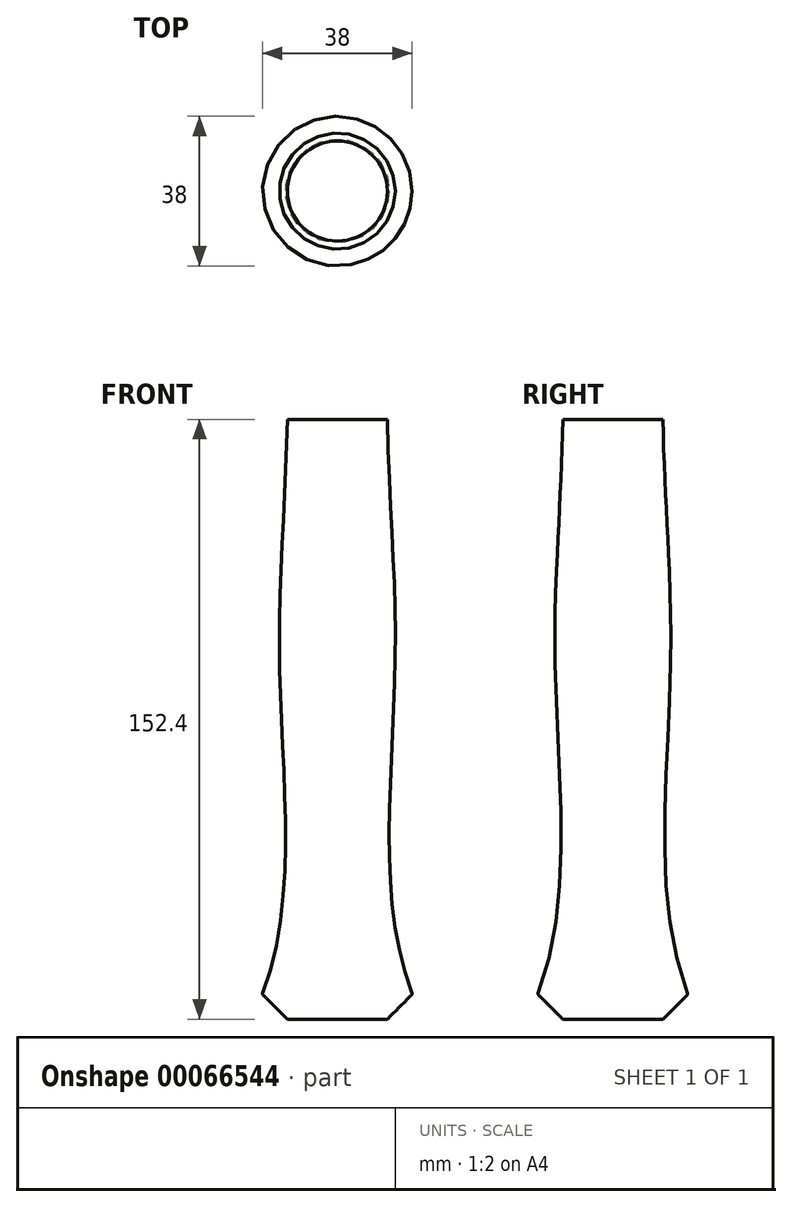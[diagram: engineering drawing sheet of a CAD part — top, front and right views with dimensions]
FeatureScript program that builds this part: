
annotation { "Feature Type Name" : "Feature", "Feature Type Description" : "" }
export const myFeature = defineFeature(function(context is Context, id is Id, definition is map)
    precondition{}
    {
        {
            var Q0;
            Q0=qCreatedBy(makeId("Front.planeOp"),FACE);
            var sketch = newSketch(context, id + "F0", { "sketchPlane" : qUnion([Q0])});
            skLineSegment(sketch, "E0", {"start": v(-26.54, 75.17) * mm, "end": v(-39.24, 75.17) * mm});
            skLineSegment(sketch, "E1", {"start": v(-26.54, -77.23) * mm, "end": v(-39.24, -77.23) * mm});
            skLineSegment(sketch, "E2", {"start": v(-45.6, -70.88) * mm, "end": v(-39.24, -77.23) * mm});
            skFitSpline(sketch, "E3.MirrorCS", {"points": [v(-39.24, 75.17) * mm, v(-41.3, 19.53) * mm, v(-39.72, -29.46) * mm, v(-45.6, -70.88) * mm], "startDerivative": vector(-4.03, -183.72) * mm, "endDerivative": vector(-47.17, -125.03) * mm});
            skLineSegment(sketch, "E4", {"start": v(-26.54, 75.17) * mm, "end": v(-26.54, -77.23) * mm, "construction": true});
            skLineSegment(sketch, "E5", {"start": v(-26.54, 75.17) * mm, "end": v(-26.54, -77.23) * mm});
            skSolve(sketch);
        }
        {
            var Q0;
            Q0=qSketchRegion(id+"F0",true);
            var Q1;
            Q1=sQuery(id+"F0.wireOp",EDGE,"E4");
            revolve(context, id + "F1", {"entities" : qUnion([Q0]), "axis" : qUnion([Q1]), "revolveType" : RevolveType.FULL});
        }
        {
            var Q0;
            Q0=makeQuery(id+"F1.opRevolve","SWEPT_EDGE",EDGE,{"disambiguationData":[OSD([sQuery(id+"F0.wireOp",EDGE,"E2"),sQuery(id+"F0.wireOp",EDGE,"E3.MirrorCS")])]});
            fillet(context, id + "F2", {"entities" : qUnion([Q0]), "radius" : 0.32 * mm, "tangentPropagation" : true, "allowEdgeOverflow" : false});
        }
    });
